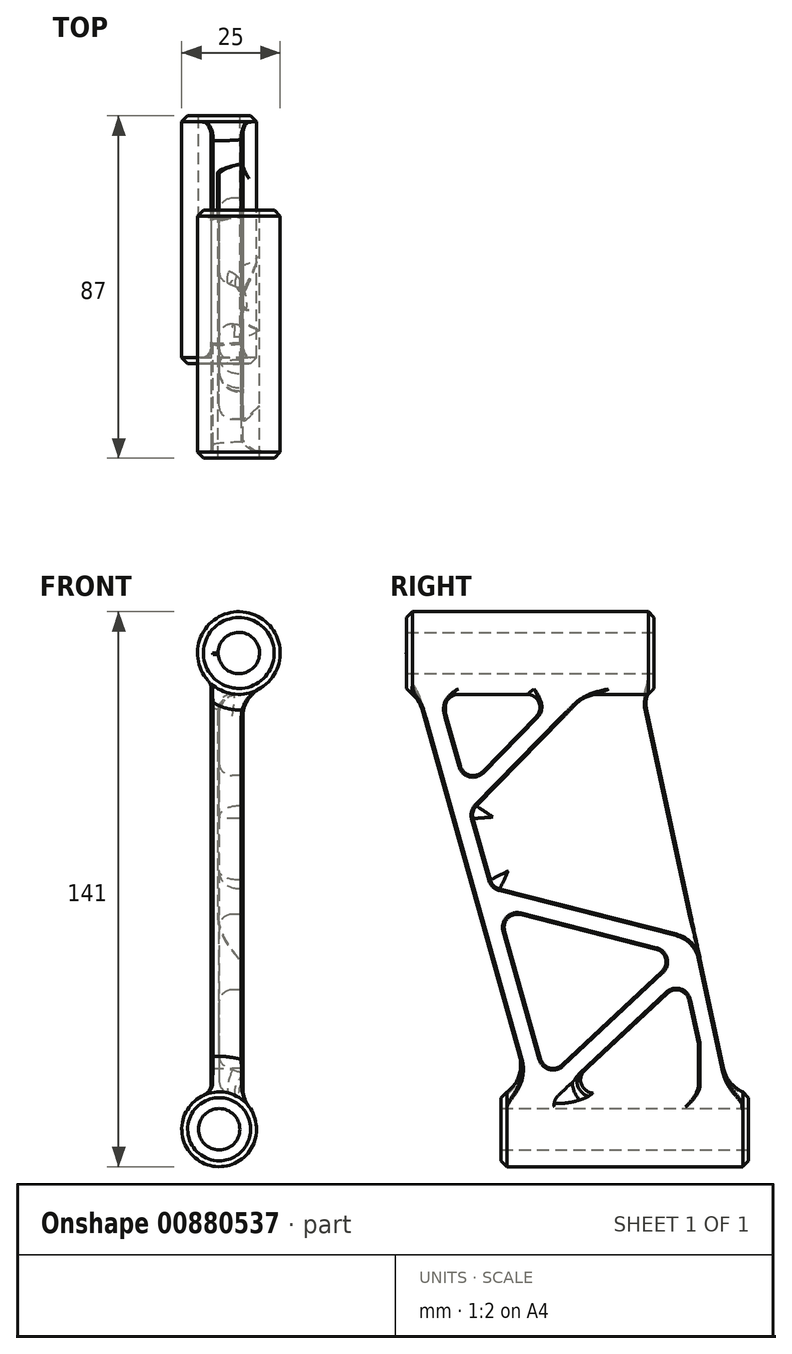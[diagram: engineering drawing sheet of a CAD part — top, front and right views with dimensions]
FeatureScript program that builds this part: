
annotation { "Feature Type Name" : "Feature", "Feature Type Description" : "" }
export const myFeature = defineFeature(function(context is Context, id is Id, definition is map)
    precondition{}
    {
        {
            var Q0;
            Q0=qCreatedBy(makeId("Right.planeOp"),FACE);
            cPlane(context, id + "F0", {"entities" : qUnion([Q0]), "cplaneType" : CPlaneType.OFFSET, "offset" : 50 * mm, "oppositeDirection" : true, "width" : 150 * mm, "height" : 150 * mm});
        }
        {
            assignVariable(context, id + "F1", {"name" : "o_ObenUnten", "anyValue" : 24});
        }
        {
            assignVariable(context, id + "F2", {"name" : "Rippenstaerke", "anyValue" : 5});
        }
        {
            assignVariable(context, id + "F3", {"name" : "Innenradien", "anyValue" : 3.3});
        }
        {
            assignVariable(context, id + "F4", {"name" : "Aussenradien", "anyValue" : getVariable(context, 'Innenradien') + getVariable(context, 'Rippenstaerke')});
        }
        {
            var Q0;
            Q0=qCreatedBy(makeId("Front.planeOp"),FACE);
            cPlane(context, id + "F5", {"entities" : qUnion([Q0]), "cplaneType" : CPlaneType.OFFSET, "offset" : getVariable(context, 'o_ObenUnten') * mm, "oppositeDirection" : true, "width" : 150 * mm, "height" : 150 * mm});
        }
        {
            var Q0;
            Q0=qCreatedBy(makeId("Right.planeOp"),FACE);
            cPlane(context, id + "F6", {"entities" : qUnion([Q0]), "cplaneType" : CPlaneType.OFFSET, "offset" : 7 * mm, "oppositeDirection" : true, "width" : 150 * mm, "height" : 150 * mm});
        }
        {
            var Q0;
            Q0=qCreatedBy(id+"F6.planeOp",FACE);
            cPlane(context, id + "F7", {"entities" : qUnion([Q0]), "cplaneType" : CPlaneType.OFFSET, "offset" : 2 * mm, "width" : 150 * mm, "height" : 150 * mm});
        }
        {
            var Q0;
            Q0=qCreatedBy(makeId("Right.planeOp"),FACE);
            var sketch = newSketch(context, id + "F8", { "sketchPlane" : qUnion([Q0])});
            skPoint(sketch, "E0", {"position": v(34.25, -63.07) * mm});
            skSolve(sketch);
        }
        {
            var Q0;
            Q0=qCreatedBy(makeId("Top.planeOp"),FACE);
            var sketch = newSketch(context, id + "F9", { "sketchPlane" : qUnion([Q0])});
            skPoint(sketch, "E1", {"position": v(55.98, 30.4) * mm});
            skSolve(sketch);
        }
        {
            var Q0;
            Q0=qCreatedBy(makeId("Front.planeOp"),FACE);
            var sketch = newSketch(context, id + "F10", { "sketchPlane" : qUnion([Q0])});
            skPoint(sketch, "E2", {"position": v(72.82, 149.27) * mm});
            skSolve(sketch);
        }
        {
            var Q0;
            Q0=qCreatedBy(makeId("Front.planeOp"),FACE);
            var sketch = newSketch(context, id + "F11", { "sketchPlane" : qUnion([Q0])});
            skCircle(sketch, "E3", {"center": v(0, 60.5) * mm, "radius": 10.5 * mm});
            skLineSegment(sketch, "E4", {"start": v(-48.92, 0) * mm, "end": v(59.28, 0) * mm, "construction": true});
            skSolve(sketch);
        }
        {
            var Q0;
            Q0=qCreatedBy(id+"F5.planeOp",FACE);
            var sketch = newSketch(context, id + "F12", { "sketchPlane" : qUnion([Q0])});
            skCircle(sketch, "E5", {"center": v(-5, -60.5) * mm, "radius": 9.5 * mm});
            skSolve(sketch);
        }
        {
            var Q0;
            Q0=sQuery(id+"F10.wireOp",VERTEX,"E2");
            var Q1;
            Q1=sQuery(id+"F8.wireOp",VERTEX,"E0");
            var Q2;
            Q2=sQuery(id+"F9.wireOp",VERTEX,"E1");
            cPlane(context, id + "F13", {"entities" : qUnion([Q0, Q1, Q2]), "cplaneType" : CPlaneType.THREE_POINT, "offset" : 25 * mm, "width" : 150 * mm, "height" : 150 * mm});
        }
        {
            var Q0;
            Q0=qCreatedBy(id+"F13.planeOp",FACE);
            var sketch = newSketch(context, id + "F14", { "sketchPlane" : qUnion([Q0])});
            skCircle(sketch, "E6", {"center": v(-47.46, 23.88) * mm, "radius": 40 * mm});
            skSolve(sketch);
        }
        {
            var Q0;
            Q0=makeQuery(id+"F14.imprint","IMPRINT",FACE,{"disambiguationData":[TD([[makeQuery(id+"F14.imprint","IMPRINT",EDGE,{"derivedFrom":sQuery(id+"F14.wireOp",EDGE,"E6")}),1.0]])]});
            var Q1;
            Q1=sQuery(id+"F14.wireOp",EDGE,"E6");
            extrude(context, id + "F15", {"entities" : qUnion([Q0]), "bodyType" : ToolBodyType.SURFACE, "surfaceEntities" : qUnion([Q1]), "endBound" : BoundingType.SYMMETRIC, "oppositeDirection" : true, "depth" : 78.48 * mm, "offsetDistance" : 25 * mm});
        }
        {
            var Q0;
            Q0=qCreatedBy(id+"F6.planeOp",FACE);
            var sketch = newSketch(context, id + "F16", { "sketchPlane" : qUnion([Q0])});
            skLineSegment(sketch, "E7", {"start": v(-63, 60.5) * mm, "end": v(-29, -60.5) * mm});
            skLineSegment(sketch, "E8", {"start": v(-29, -60.5) * mm, "end": v(21, -60.5) * mm});
            skLineSegment(sketch, "E9", {"start": v(21, -60.5) * mm, "end": v(-5, 60.5) * mm});
            skLineSegment(sketch, "E10", {"start": v(-5, 60.5) * mm, "end": v(-63, 60.5) * mm});
            skSolve(sketch);
        }
        {
            var Q0;
            Q0=makeQuery(id+"F16.imprint","IMPRINT",FACE,{"disambiguationData":[TD([[makeQuery(id+"F16.imprint","IMPRINT",EDGE,{"derivedFrom":sQuery(id+"F16.wireOp",EDGE,"E7")}),1.0]])]});
            extrude(context, id + "F17", {"entities" : qUnion([Q0]), "depth" : 8 * mm, "offsetDistance" : 25 * mm});
        }
        {
            var Q0;
            Q0=qCreatedBy(id+"F7.planeOp",FACE);
            var sketch = newSketch(context, id + "F18", { "sketchPlane" : qUnion([Q0])});
            skLineSegment(sketch, "E11", {"start": v(-52.94, 45.06) * mm, "end": v(-49.2, 31.75) * mm});
            skLineSegment(sketch, "E12", {"start": v(-43.66, 30.34) * mm, "end": v(-11.8, 62.98) * mm});
            skLineSegment(sketch, "E13", {"start": v(-1.21, 66.67) * mm, "end": v(-45.17, 21.63) * mm});
            skLineSegment(sketch, "E14", {"start": v(-45.98, 18.43) * mm, "end": v(-41.6, 2.84) * mm});
            skLineSegment(sketch, "E15", {"start": v(-39.24, 0.54) * mm, "end": v(16.03, -13.55) * mm});
            skLineSegment(sketch, "E16", {"start": v(16.03, -13.55) * mm, "end": v(-1.21, 66.67) * mm});
            skLineSegment(sketch, "E17", {"start": v(-37.98, -10.05) * mm, "end": v(-28.82, -42.64) * mm});
            skLineSegment(sketch, "E18", {"start": v(0.54, -14.77) * mm, "end": v(-33.99, -5.96) * mm});
            skLineSegment(sketch, "E19", {"start": v(-23.4, -44.16) * mm, "end": v(1.99, -20.37) * mm});
            skLineSegment(sketch, "E20", {"start": v(3.35, -25.95) * mm, "end": v(-24.37, -51.92) * mm});
            skLineSegment(sketch, "E21", {"start": v(11.2, -38.68) * mm, "end": v(8.83, -27.66) * mm});
            skLineSegment(sketch, "E22", {"start": v(-10.85, 65.29) * mm, "end": v(-10.85, 65.5) * mm});
            skLineSegment(sketch, "E23", {"start": v(-53.06, 45.95) * mm, "end": v(-53.06, 65.5) * mm});
            skLineSegment(sketch, "E24", {"start": v(-22.4, -65.5) * mm, "end": v(-25.29, -55.22) * mm});
            skLineSegment(sketch, "E25", {"start": v(11.27, -39.37) * mm, "end": v(11.27, -65.5) * mm});
            skLineSegment(sketch, "E26", {"start": v(-10.85, 65.5) * mm, "end": v(-53.06, 65.5) * mm});
            skLineSegment(sketch, "E27", {"start": v(11.27, -65.5) * mm, "end": v(-22.4, -65.5) * mm});
            skPoint(sketch, "E28.visualSharp", {"position": v(-41.1, 1) * mm});
            skArc(sketch, "E28.filletArc", {"start": v(-41.6, 2.84) * mm, "mid": v(-40.73, 1.38) * mm, "end": v(-39.24, 0.54) * mm});
            skPoint(sketch, "E29.visualSharp", {"position": v(-39.53, -4.55) * mm});
            skArc(sketch, "E29.filletArc", {"start": v(-33.99, -5.96) * mm, "mid": v(-37.17, -6.85) * mm, "end": v(-37.98, -10.05) * mm});
            skPoint(sketch, "E30.visualSharp", {"position": v(-27.36, -47.87) * mm});
            skArc(sketch, "E30.filletArc", {"start": v(-28.82, -42.64) * mm, "mid": v(-26.53, -44.93) * mm, "end": v(-23.4, -44.16) * mm});
            skPoint(sketch, "E31.visualSharp", {"position": v(6.38, -16.25) * mm});
            skArc(sketch, "E31.filletArc", {"start": v(1.99, -20.37) * mm, "mid": v(2.92, -17.14) * mm, "end": v(0.54, -14.77) * mm});
            skPoint(sketch, "E32.visualSharp", {"position": v(7.6, -21.96) * mm});
            skArc(sketch, "E32.filletArc", {"start": v(8.83, -27.66) * mm, "mid": v(6.59, -25.2) * mm, "end": v(3.35, -25.95) * mm});
            skPoint(sketch, "E33.visualSharp", {"position": v(-25.83, -53.3) * mm});
            skArc(sketch, "E33.filletArc", {"start": v(-24.37, -51.92) * mm, "mid": v(-25.3, -53.45) * mm, "end": v(-25.29, -55.22) * mm});
            skPoint(sketch, "E34.visualSharp", {"position": v(11.27, -39.02) * mm});
            skArc(sketch, "E34.filletArc", {"start": v(11.27, -39.37) * mm, "mid": v(11.25, -39.03) * mm, "end": v(11.2, -38.68) * mm});
            skPoint(sketch, "E35.visualSharp", {"position": v(-46.5, 20.26) * mm});
            skArc(sketch, "E35.filletArc", {"start": v(-45.17, 21.63) * mm, "mid": v(-46, 20.14) * mm, "end": v(-45.98, 18.43) * mm});
            skPoint(sketch, "E36.visualSharp", {"position": v(-47.65, 26.25) * mm});
            skArc(sketch, "E36.filletArc", {"start": v(-49.2, 31.75) * mm, "mid": v(-46.83, 29.44) * mm, "end": v(-43.66, 30.34) * mm});
            skPoint(sketch, "E37.visualSharp", {"position": v(-53.06, 45.5) * mm});
            skArc(sketch, "E37.filletArc", {"start": v(-53.06, 45.95) * mm, "mid": v(-53.03, 45.5) * mm, "end": v(-52.94, 45.06) * mm});
            skPoint(sketch, "E38.visualSharp", {"position": v(-10.85, 63.94) * mm});
            skArc(sketch, "E38.filletArc", {"start": v(-11.8, 62.98) * mm, "mid": v(-11.1, 64.04) * mm, "end": v(-10.85, 65.29) * mm});
            skSolve(sketch);
        }
        {
            var Q0;
            Q0=makeQuery(id+"F18.imprint","IMPRINT",FACE,{"disambiguationData":[TD([[makeQuery(id+"F18.imprint","IMPRINT",EDGE,{"derivedFrom":sQuery(id+"F18.wireOp",EDGE,"E11")}),1.0]])]});
            var Q1;
            Q1=makeQuery(id+"F18.imprint","IMPRINT",FACE,{"disambiguationData":[TD([[makeQuery(id+"F18.imprint","IMPRINT",EDGE,{"derivedFrom":sQuery(id+"F18.wireOp",EDGE,"E13")}),1.0]])]});
            var Q2;
            Q2=makeQuery(id+"F18.imprint","IMPRINT",FACE,{"disambiguationData":[TD([[makeQuery(id+"F18.imprint","IMPRINT",EDGE,{"derivedFrom":sQuery(id+"F18.wireOp",EDGE,"E17")}),1.0]])]});
            var Q3;
            Q3=makeQuery(id+"F18.imprint","IMPRINT",FACE,{"disambiguationData":[TD([[makeQuery(id+"F18.imprint","IMPRINT",EDGE,{"derivedFrom":sQuery(id+"F18.wireOp",EDGE,"E20")}),1.0]])]});
            extrude(context, id + "F19", {"entities" : qUnion([Q0, Q1, Q2, Q3]), "operationType" : NewBodyOperationType.REMOVE, "depth" : 25 * mm, "offsetDistance" : 25 * mm});
        }
        {
            var Q0;
            Q0=makeQuery(id+"F11.imprint","IMPRINT",FACE,{"disambiguationData":[TD([[makeQuery(id+"F11.imprint","IMPRINT",EDGE,{"derivedFrom":sQuery(id+"F11.wireOp",EDGE,"E3")}),1.0]])]});
            var Q1;
            Q1=makeQuery(id+"F12.imprint","IMPRINT",FACE,{"disambiguationData":[TD([[makeQuery(id+"F12.imprint","IMPRINT",EDGE,{"derivedFrom":sQuery(id+"F12.wireOp",EDGE,"E5")}),1.0]])]});
            extrude(context, id + "F20", {"entities" : qUnion([Q0, Q1]), "operationType" : NewBodyOperationType.ADD, "depth" : 62.9 * mm, "offsetDistance" : 25 * mm});
        }
        {
            var Q0;
            Q0=makeQuery(id+"F20.opExtrude","CAP_EDGE",EDGE,{"disambiguationData":[OSD([sQuery(id+"F11.wireOp",EDGE,"E3")])],"isStart":false});
            var Q1;
            Q1=makeQuery(id+"F20.opExtrude","CAP_EDGE",EDGE,{"disambiguationData":[OSD([sQuery(id+"F12.wireOp",EDGE,"E5")])],"isStart":false});
            var Q2;
            Q2=makeQuery(id+"F20.opExtrude","CAP_EDGE",EDGE,{"disambiguationData":[OSD([sQuery(id+"F12.wireOp",EDGE,"E5")])],"isStart":true});
            var Q3;
            Q3=makeQuery(id+"F20.opExtrude","CAP_EDGE",EDGE,{"disambiguationData":[OSD([sQuery(id+"F11.wireOp",EDGE,"E3")])],"isStart":true});
            chamfer(context, id + "F21", {"entities" : qUnion([Q0, Q1, Q2, Q3]), "width" : 1.5 * mm, "tangentPropagation" : true});
        }
        {
            var Q0;
            Q0=makeQuery(id+"F19.boolean.opBoolean","INTERSECT",EDGE,{"derivedFrom":[makeQuery(id+"F17.opExtrude","SWEPT_FACE",FACE,{"disambiguationData":[OSD([sQuery(id+"F16.wireOp",EDGE,"E9")])]}),makeQuery(id+"F19.opExtrude","SWEPT_FACE",FACE,{"disambiguationData":[OSD([sQuery(id+"F18.wireOp",EDGE,"E15")])]})]});
            var Q1;
            Q1=makeQuery(id+"F20.boolean.opBoolean","INTERSECT",EDGE,{"derivedFrom":[makeQuery(id+"F17.opExtrude","SWEPT_FACE",FACE,{"disambiguationData":[OSD([sQuery(id+"F16.wireOp",EDGE,"E9")])]}),makeQuery(id+"F20.opExtrude","SWEPT_FACE",FACE,{"disambiguationData":[OSD([sQuery(id+"F12.wireOp",EDGE,"E5")])]})]});
            var Q2;
            Q2=makeQuery(id+"F20.boolean.opBoolean","INTERSECT",EDGE,{"derivedFrom":[makeQuery(id+"F17.opExtrude","SWEPT_FACE",FACE,{"disambiguationData":[OSD([sQuery(id+"F16.wireOp",EDGE,"E7")])]}),makeQuery(id+"F20.opExtrude","SWEPT_FACE",FACE,{"disambiguationData":[OSD([sQuery(id+"F11.wireOp",EDGE,"E3")])]})]});
            var Q3;
            Q3=makeQuery(id+"F20.boolean.opBoolean","INTERSECT",EDGE,{"derivedFrom":[makeQuery(id+"F17.opExtrude","SWEPT_FACE",FACE,{"disambiguationData":[OSD([sQuery(id+"F16.wireOp",EDGE,"E7")])]}),makeQuery(id+"F20.opExtrude","SWEPT_FACE",FACE,{"disambiguationData":[OSD([sQuery(id+"F12.wireOp",EDGE,"E5")])]})]});
            var Q4;
            Q4=makeQuery(id+"F20.boolean.opBoolean","INTERSECT",EDGE,{"derivedFrom":[makeQuery(id+"F19.boolean.opBoolean","COPY",FACE,{"derivedFrom":makeQuery(id+"F19.opExtrude","SWEPT_FACE",FACE,{"disambiguationData":[OSD([sQuery(id+"F18.wireOp",EDGE,"E13")])]})}),makeQuery(id+"F20.opExtrude","SWEPT_FACE",FACE,{"disambiguationData":[OSD([sQuery(id+"F11.wireOp",EDGE,"E3")])]})]});
            var Q5;
            Q5=makeQuery(id+"F20.boolean.opBoolean","INTERSECT",EDGE,{"disambiguationData":[OD(0.0)],"derivedFrom":[makeQuery(id+"F17.opExtrude","CAP_FACE",FACE,{"disambiguationData":[OSD([sQuery(id+"F16.wireOp",EDGE,"E7"),sQuery(id+"F16.wireOp",EDGE,"E8"),sQuery(id+"F16.wireOp",EDGE,"E9"),sQuery(id+"F16.wireOp",EDGE,"E10")])],"isStart":false}),makeQuery(id+"F20.opExtrude","SWEPT_FACE",FACE,{"disambiguationData":[OSD([sQuery(id+"F11.wireOp",EDGE,"E3")])]})]});
            var Q6;
            Q6=makeQuery(id+"F20.boolean.opBoolean","INTERSECT",EDGE,{"disambiguationData":[OD(1.0)],"derivedFrom":[makeQuery(id+"F17.opExtrude","CAP_FACE",FACE,{"disambiguationData":[OSD([sQuery(id+"F16.wireOp",EDGE,"E7"),sQuery(id+"F16.wireOp",EDGE,"E8"),sQuery(id+"F16.wireOp",EDGE,"E9"),sQuery(id+"F16.wireOp",EDGE,"E10")])],"isStart":false}),makeQuery(id+"F20.opExtrude","SWEPT_FACE",FACE,{"disambiguationData":[OSD([sQuery(id+"F11.wireOp",EDGE,"E3")])]})]});
            var Q7;
            Q7=makeQuery(id+"F20.boolean.opBoolean","INTERSECT",EDGE,{"disambiguationData":[OD(0.0)],"derivedFrom":[makeQuery(id+"F17.opExtrude","CAP_FACE",FACE,{"disambiguationData":[OSD([sQuery(id+"F16.wireOp",EDGE,"E7"),sQuery(id+"F16.wireOp",EDGE,"E8"),sQuery(id+"F16.wireOp",EDGE,"E9"),sQuery(id+"F16.wireOp",EDGE,"E10")])],"isStart":false}),makeQuery(id+"F20.opExtrude","SWEPT_FACE",FACE,{"disambiguationData":[OSD([sQuery(id+"F12.wireOp",EDGE,"E5")])]})]});
            var Q8;
            Q8=makeQuery(id+"F20.boolean.opBoolean","INTERSECT",EDGE,{"disambiguationData":[OD(1.0)],"derivedFrom":[makeQuery(id+"F17.opExtrude","CAP_FACE",FACE,{"disambiguationData":[OSD([sQuery(id+"F16.wireOp",EDGE,"E7"),sQuery(id+"F16.wireOp",EDGE,"E8"),sQuery(id+"F16.wireOp",EDGE,"E9"),sQuery(id+"F16.wireOp",EDGE,"E10")])],"isStart":false}),makeQuery(id+"F20.opExtrude","SWEPT_FACE",FACE,{"disambiguationData":[OSD([sQuery(id+"F12.wireOp",EDGE,"E5")])]})]});
            fillet(context, id + "F22", {"entities" : qUnion([Q0, Q1, Q2, Q3, Q4, Q5, Q6, Q7, Q8]), "radius" : getVariable(context, 'Aussenradien') * mm, "tangentPropagation" : true, "allowEdgeOverflow" : false});
        }
        {
            var Q0;
            Q0=makeQuery(id+"F20.boolean.opBoolean","INTERSECT",EDGE,{"derivedFrom":[makeQuery(id+"F19.boolean.opBoolean","COPY",FACE,{"derivedFrom":makeQuery(id+"F19.opExtrude","SWEPT_FACE",FACE,{"disambiguationData":[OSD([sQuery(id+"F18.wireOp",EDGE,"E12")])]})}),makeQuery(id+"F20.opExtrude","SWEPT_FACE",FACE,{"disambiguationData":[OSD([sQuery(id+"F11.wireOp",EDGE,"E3")])]})]});
            var Q1;
            Q1=makeQuery(id+"F20.boolean.opBoolean","INTERSECT",EDGE,{"derivedFrom":[makeQuery(id+"F19.boolean.opBoolean","COPY",FACE,{"derivedFrom":makeQuery(id+"F19.opExtrude","SWEPT_FACE",FACE,{"disambiguationData":[OSD([sQuery(id+"F18.wireOp",EDGE,"E23")])]})}),makeQuery(id+"F20.opExtrude","SWEPT_FACE",FACE,{"disambiguationData":[OSD([sQuery(id+"F11.wireOp",EDGE,"E3")])]})]});
            var Q2;
            Q2=makeQuery(id+"F20.boolean.opBoolean","INTERSECT",EDGE,{"derivedFrom":[makeQuery(id+"F19.boolean.opBoolean","COPY",FACE,{"derivedFrom":makeQuery(id+"F19.opExtrude","SWEPT_FACE",FACE,{"disambiguationData":[OSD([sQuery(id+"F18.wireOp",EDGE,"E25")])]})}),makeQuery(id+"F20.opExtrude","SWEPT_FACE",FACE,{"disambiguationData":[OSD([sQuery(id+"F12.wireOp",EDGE,"E5")])]})]});
            var Q3;
            Q3=makeQuery(id+"F20.boolean.opBoolean","INTERSECT",EDGE,{"derivedFrom":[makeQuery(id+"F19.boolean.opBoolean","COPY",FACE,{"derivedFrom":makeQuery(id+"F19.opExtrude","SWEPT_FACE",FACE,{"disambiguationData":[OSD([sQuery(id+"F18.wireOp",EDGE,"E20")])]})}),makeQuery(id+"F20.opExtrude","SWEPT_FACE",FACE,{"disambiguationData":[OSD([sQuery(id+"F12.wireOp",EDGE,"E5")])]})]});
            fillet(context, id + "F23", {"entities" : qUnion([Q0, Q1, Q2, Q3]), "radius" : getVariable(context, 'Innenradien') * mm, "allowEdgeOverflow" : false});
        }
        {
            var Q0;
            Q0=makeQuery(id+"F19.boolean.opBoolean","COPY",FACE,{"derivedFrom":makeQuery(id+"F19.opExtrude","CAP_FACE",FACE,{"disambiguationData":[OSD([sQuery(id+"F18.wireOp",EDGE,"E20"),sQuery(id+"F18.wireOp",EDGE,"E21"),sQuery(id+"F18.wireOp",EDGE,"E24"),sQuery(id+"F18.wireOp",EDGE,"E25"),sQuery(id+"F18.wireOp",EDGE,"E27"),sQuery(id+"F18.wireOp",EDGE,"E32.filletArc"),sQuery(id+"F18.wireOp",EDGE,"E33.filletArc"),sQuery(id+"F18.wireOp",EDGE,"E34.filletArc")])],"isStart":true})});
            var Q1;
            Q1=makeQuery(id+"F19.boolean.opBoolean","COPY",FACE,{"derivedFrom":makeQuery(id+"F19.opExtrude","CAP_FACE",FACE,{"disambiguationData":[OSD([sQuery(id+"F18.wireOp",EDGE,"E17"),sQuery(id+"F18.wireOp",EDGE,"E18"),sQuery(id+"F18.wireOp",EDGE,"E19"),sQuery(id+"F18.wireOp",EDGE,"E29.filletArc"),sQuery(id+"F18.wireOp",EDGE,"E30.filletArc"),sQuery(id+"F18.wireOp",EDGE,"E31.filletArc")])],"isStart":true})});
            var Q2;
            Q2=makeQuery(id+"F19.boolean.opBoolean","COPY",FACE,{"derivedFrom":makeQuery(id+"F19.opExtrude","CAP_FACE",FACE,{"disambiguationData":[OSD([sQuery(id+"F18.wireOp",EDGE,"E11"),sQuery(id+"F18.wireOp",EDGE,"E12"),sQuery(id+"F18.wireOp",EDGE,"E22"),sQuery(id+"F18.wireOp",EDGE,"E23"),sQuery(id+"F18.wireOp",EDGE,"E26"),sQuery(id+"F18.wireOp",EDGE,"E36.filletArc"),sQuery(id+"F18.wireOp",EDGE,"E37.filletArc"),sQuery(id+"F18.wireOp",EDGE,"E38.filletArc")])],"isStart":true})});
            var Q3;
            Q3=makeQuery(id+"F20.boolean.opBoolean","INTERSECT",EDGE,{"derivedFrom":[makeQuery(id+"F17.opExtrude","CAP_FACE",FACE,{"disambiguationData":[OSD([sQuery(id+"F16.wireOp",EDGE,"E7"),sQuery(id+"F16.wireOp",EDGE,"E8"),sQuery(id+"F16.wireOp",EDGE,"E9"),sQuery(id+"F16.wireOp",EDGE,"E10")])],"isStart":true}),makeQuery(id+"F20.opExtrude","SWEPT_FACE",FACE,{"disambiguationData":[OSD([sQuery(id+"F11.wireOp",EDGE,"E3")])]})]});
            var Q4;
            Q4=makeQuery(id+"F20.boolean.opBoolean","INTERSECT",EDGE,{"derivedFrom":[makeQuery(id+"F17.opExtrude","CAP_FACE",FACE,{"disambiguationData":[OSD([sQuery(id+"F16.wireOp",EDGE,"E7"),sQuery(id+"F16.wireOp",EDGE,"E8"),sQuery(id+"F16.wireOp",EDGE,"E9"),sQuery(id+"F16.wireOp",EDGE,"E10")])],"isStart":true}),makeQuery(id+"F20.opExtrude","SWEPT_FACE",FACE,{"disambiguationData":[OSD([sQuery(id+"F12.wireOp",EDGE,"E5")])]})]});
            fillet(context, id + "F24", {"entities" : qUnion([Q0, Q1, Q2, Q3, Q4]), "radius" : getVariable(context, 'Innenradien') * mm, "tangentPropagation" : true, "allowEdgeOverflow" : false});
        }
        {
            var Q0;
            Q0=makeQuery(id+"F19.boolean.opBoolean","COPY",EDGE,{"derivedFrom":makeQuery(id+"F19.opExtrude","CAP_EDGE",EDGE,{"disambiguationData":[OSD([sQuery(id+"F18.wireOp",EDGE,"E13")])],"isStart":true})});
            fillet(context, id + "F25", {"entities" : qUnion([Q0]), "radius" : 5 * mm, "tangentPropagation" : true, "allowEdgeOverflow" : false});
        }
        {
            var Q0;
            Q0=makeQuery(id+"F20.boolean.opBoolean","INTERSECT",EDGE,{"derivedFrom":[makeQuery(id+"F17.opExtrude","SWEPT_FACE",FACE,{"disambiguationData":[OSD([sQuery(id+"F16.wireOp",EDGE,"E9")])]}),makeQuery(id+"F20.opExtrude","SWEPT_FACE",FACE,{"disambiguationData":[OSD([sQuery(id+"F11.wireOp",EDGE,"E3")])]})]});
            fillet(context, id + "F26", {"entities" : qUnion([Q0]), "radius" : 8.3 * mm, "tangentPropagation" : true, "allowEdgeOverflow" : false});
        }
        {
            var Q0;
            Q0=makeQuery(id+"F17.opExtrude","CAP_EDGE",EDGE,{"disambiguationData":[OSD([sQuery(id+"F16.wireOp",EDGE,"E7")])],"isStart":true});
            var Q1;
            Q1=makeQuery(id+"F17.opExtrude","CAP_EDGE",EDGE,{"disambiguationData":[OSD([sQuery(id+"F16.wireOp",EDGE,"E7")])],"isStart":false});
            var Q2;
            Q2=makeQuery(id+"F19.boolean.opBoolean","INTERSECT",EDGE,{"derivedFrom":[makeQuery(id+"F17.opExtrude","CAP_FACE",FACE,{"disambiguationData":[OSD([sQuery(id+"F16.wireOp",EDGE,"E7"),sQuery(id+"F16.wireOp",EDGE,"E8"),sQuery(id+"F16.wireOp",EDGE,"E9"),sQuery(id+"F16.wireOp",EDGE,"E10")])],"isStart":false}),makeQuery(id+"F19.opExtrude","SWEPT_FACE",FACE,{"disambiguationData":[OSD([sQuery(id+"F18.wireOp",EDGE,"E18")])]})]});
            var Q3;
            Q3=makeQuery(id+"F19.boolean.opBoolean","INTERSECT",EDGE,{"derivedFrom":[makeQuery(id+"F17.opExtrude","CAP_FACE",FACE,{"disambiguationData":[OSD([sQuery(id+"F16.wireOp",EDGE,"E7"),sQuery(id+"F16.wireOp",EDGE,"E8"),sQuery(id+"F16.wireOp",EDGE,"E9"),sQuery(id+"F16.wireOp",EDGE,"E10")])],"isStart":false}),makeQuery(id+"F19.opExtrude","SWEPT_FACE",FACE,{"disambiguationData":[OSD([sQuery(id+"F18.wireOp",EDGE,"E15")])]})]});
            var Q4;
            Q4=makeQuery(id+"F19.boolean.opBoolean","INTERSECT",EDGE,{"derivedFrom":[makeQuery(id+"F17.opExtrude","CAP_FACE",FACE,{"disambiguationData":[OSD([sQuery(id+"F16.wireOp",EDGE,"E7"),sQuery(id+"F16.wireOp",EDGE,"E8"),sQuery(id+"F16.wireOp",EDGE,"E9"),sQuery(id+"F16.wireOp",EDGE,"E10")])],"isStart":false}),makeQuery(id+"F19.opExtrude","SWEPT_FACE",FACE,{"disambiguationData":[OSD([sQuery(id+"F18.wireOp",EDGE,"E20")])]})]});
            var Q5;
            Q5=makeQuery(id+"F19.boolean.opBoolean","INTERSECT",EDGE,{"derivedFrom":[makeQuery(id+"F17.opExtrude","CAP_FACE",FACE,{"disambiguationData":[OSD([sQuery(id+"F16.wireOp",EDGE,"E7"),sQuery(id+"F16.wireOp",EDGE,"E8"),sQuery(id+"F16.wireOp",EDGE,"E9"),sQuery(id+"F16.wireOp",EDGE,"E10")])],"isStart":false}),makeQuery(id+"F19.opExtrude","SWEPT_FACE",FACE,{"disambiguationData":[OSD([sQuery(id+"F18.wireOp",EDGE,"E12")])]})]});
            var Q6;
            Q6=makeQuery(id+"F19.boolean.opBoolean","INTERSECT",EDGE,{"derivedFrom":[makeQuery(id+"F17.opExtrude","SWEPT_FACE",FACE,{"disambiguationData":[OSD([sQuery(id+"F16.wireOp",EDGE,"E9")])]}),makeQuery(id+"F19.opExtrude","CAP_FACE",FACE,{"disambiguationData":[OSD([sQuery(id+"F18.wireOp",EDGE,"E13"),sQuery(id+"F18.wireOp",EDGE,"E14"),sQuery(id+"F18.wireOp",EDGE,"E15"),sQuery(id+"F18.wireOp",EDGE,"E16"),sQuery(id+"F18.wireOp",EDGE,"E28.filletArc"),sQuery(id+"F18.wireOp",EDGE,"E35.filletArc")])],"isStart":true})]});
            var Q7;
            Q7=makeQuery(id+"F17.opExtrude","CAP_EDGE",EDGE,{"disambiguationData":[OSD([sQuery(id+"F16.wireOp",EDGE,"E9")])],"isStart":true});
            chamfer(context, id + "F27", {"entities" : qUnion([Q0, Q1, Q2, Q3, Q4, Q5, Q6, Q7]), "width" : 0.4 * mm, "tangentPropagation" : true});
        }
        {
            var Q0;
            Q0=qCreatedBy(makeId("Front.planeOp"),FACE);
            var sketch = newSketch(context, id + "F28", { "sketchPlane" : qUnion([Q0])});
            skCircle(sketch, "E39", {"center": v(0, 60.5) * mm, "radius": 5.25 * mm});
            skCircle(sketch, "E40", {"center": v(-5, -60.5) * mm, "radius": 5.25 * mm});
            skSolve(sketch);
        }
        {
            var Q0;
            Q0=makeQuery(id+"F28.imprint","IMPRINT",FACE,{"disambiguationData":[TD([[makeQuery(id+"F28.imprint","IMPRINT",EDGE,{"derivedFrom":sQuery(id+"F28.wireOp",EDGE,"E39")}),1.0]])]});
            var Q1;
            Q1=makeQuery(id+"F28.imprint","IMPRINT",FACE,{"disambiguationData":[TD([[makeQuery(id+"F28.imprint","IMPRINT",EDGE,{"derivedFrom":sQuery(id+"F28.wireOp",EDGE,"E40")}),1.0]])]});
            extrude(context, id + "F29", {"entities" : qUnion([Q0, Q1]), "operationType" : NewBodyOperationType.REMOVE, "endBound" : BoundingType.SYMMETRIC, "depth" : 179.56 * mm, "offsetDistance" : 25 * mm});
        }
        {
            var Q0;
            Q0=qCreatedBy(id+"F0.planeOp",FACE);
            var sketch = newSketch(context, id + "F30", { "sketchPlane" : qUnion([Q0])});
            skCircle(sketch, "E41", {"center": v(-75, 150.5) * mm, "radius": 12 * mm});
            skCircle(sketch, "E42", {"center": v(15, 150.5) * mm, "radius": 12 * mm});
            skLineSegment(sketch, "E43", {"start": v(55.78, 150.5) * mm, "end": v(-104.47, 150.5) * mm, "construction": true});
            skSolve(sketch);
        }
        {
            var Q0;
            Q0=qCreatedBy(makeId("Right.planeOp"),FACE);
            var sketch = newSketch(context, id + "F31", { "sketchPlane" : qUnion([Q0])});
            skLineSegment(sketch, "E44", {"start": v(0, 60.5) * mm, "end": v(-62.9, 60.5) * mm, "construction": true});
            skSolve(sketch);
        }
        {
            var Q0;
            Q0=sQuery(id+"F31.wireOp",EDGE,"E44");
            var Q1;
            Q1=sQuery(id+"F30.wireOp",EDGE,"E43");
            cPlane(context, id + "F32", {"entities" : qUnion([Q0, Q1]), "cplaneType" : CPlaneType.LINE_ANGLE, "offset" : 25 * mm, "angle" : 36.89 * degree, "width" : 150 * mm, "height" : 150 * mm});
        }
        {
            var Q0;
            Q0=sQuery(id+"F31.wireOp",EDGE,"E44");
            var Q1;
            Q1=sQuery(id+"F30.wireOp",EDGE,"E43");
            cPlane(context, id + "F33", {"entities" : qUnion([Q0, Q1]), "cplaneType" : CPlaneType.LINE_ANGLE, "offset" : 25 * mm, "angle" : 0 * degree, "width" : 150 * mm, "height" : 150 * mm});
        }
    });
